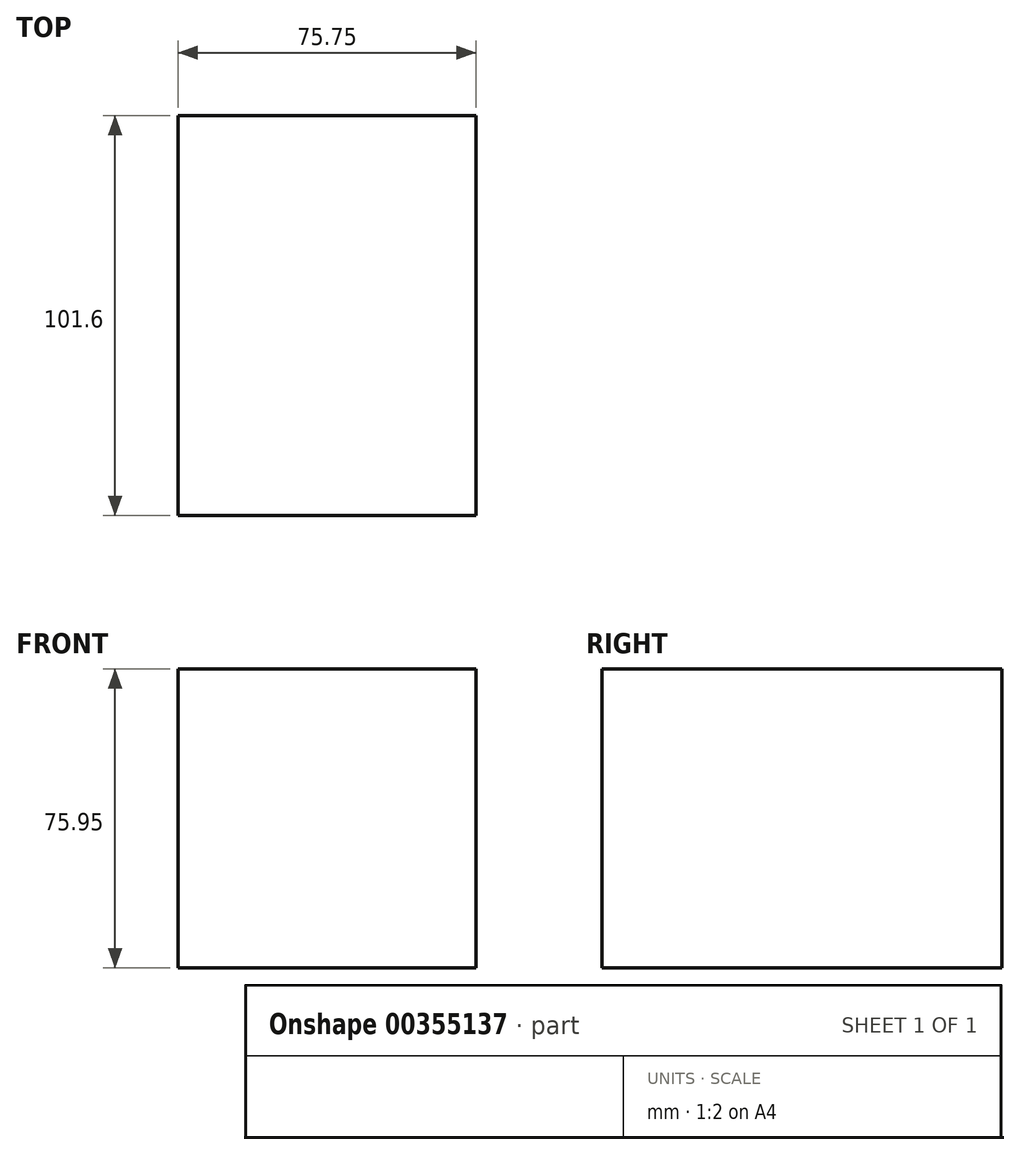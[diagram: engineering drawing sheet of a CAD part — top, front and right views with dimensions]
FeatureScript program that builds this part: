
annotation { "Feature Type Name" : "Feature", "Feature Type Description" : "" }
export const myFeature = defineFeature(function(context is Context, id is Id, definition is map)
    precondition{}
    {
        {
            var Q0;
            Q0=qCreatedBy(makeId("Front.planeOp"),FACE);
            var sketch = newSketch(context, id + "F0", { "sketchPlane" : qUnion([Q0])});
            skLineSegment(sketch, "E0.bottom", {"start": v(-75.75, 75.95) * mm, "end": v(0, 75.95) * mm});
            skLineSegment(sketch, "E0.top", {"start": v(-75.75, 0) * mm, "end": v(0, 0) * mm});
            skLineSegment(sketch, "E0.left", {"start": v(-75.75, 75.95) * mm, "end": v(-75.75, 0) * mm});
            skLineSegment(sketch, "E0.right", {"start": v(0, 75.95) * mm, "end": v(0, 0) * mm});
            skSolve(sketch);
        }
        {
            var Q0;
            Q0=makeQuery(id+"F0.imprint","IMPRINT",FACE,{"disambiguationData":[TD([[makeQuery(id+"F0.imprint","IMPRINT",EDGE,{"derivedFrom":sQuery(id+"F0.wireOp",EDGE,"E0.bottom")}),-1.0]])]});
            extrude(context, id + "F1", {"entities" : qUnion([Q0]), "depth" : 101.6 * mm});
        }
    });
